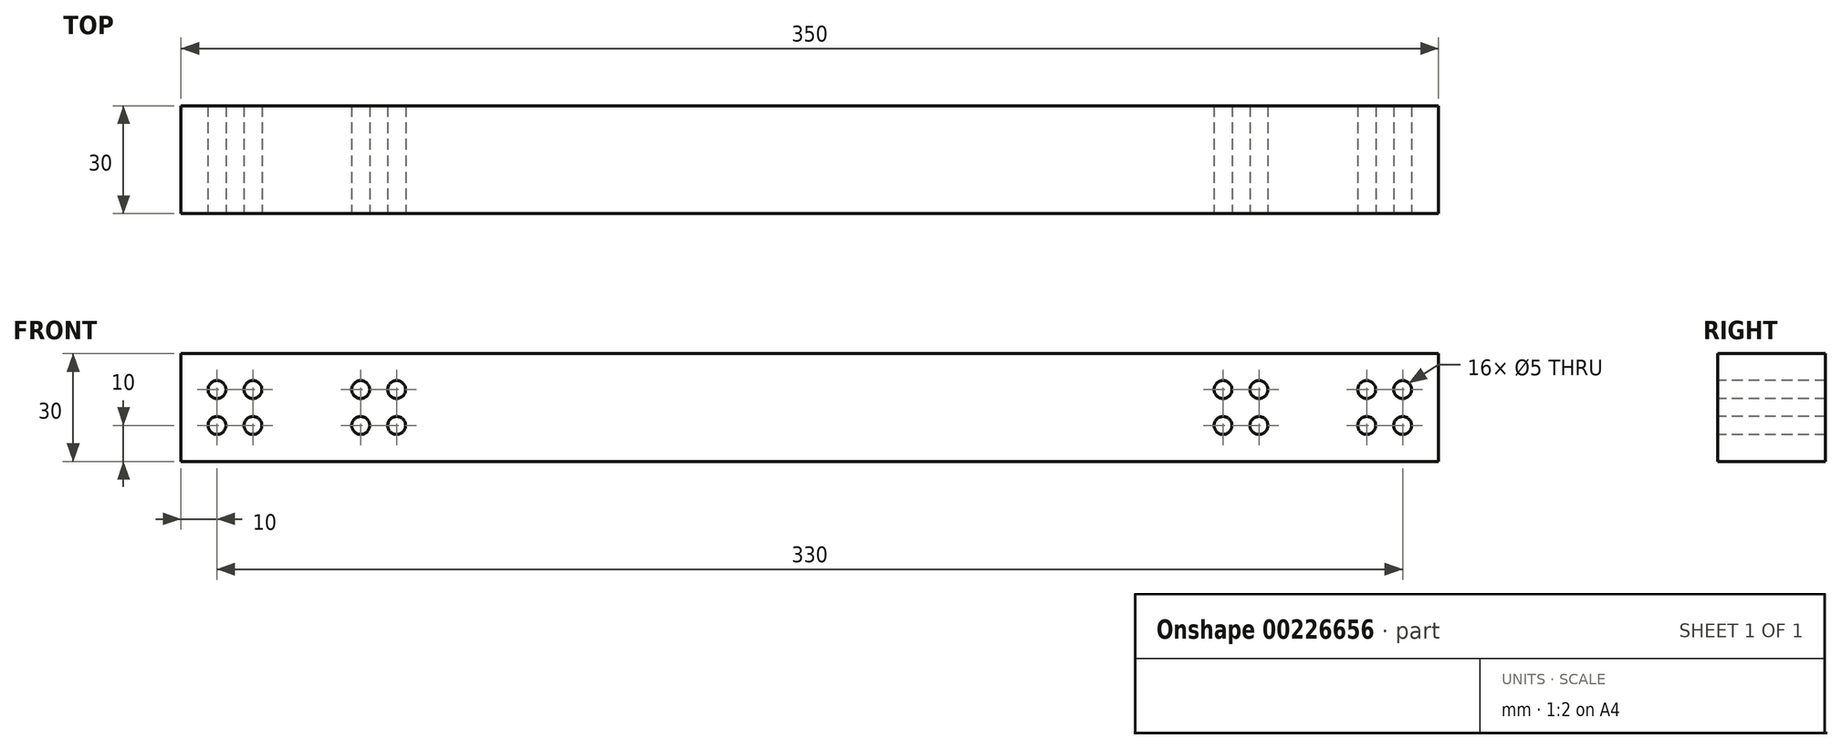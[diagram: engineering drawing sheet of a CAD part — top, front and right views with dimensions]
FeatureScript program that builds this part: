
annotation { "Feature Type Name" : "Feature", "Feature Type Description" : "" }
export const myFeature = defineFeature(function(context is Context, id is Id, definition is map)
    precondition{}
    {
        {
            var Q0;
            Q0=qCreatedBy(makeId("Front.planeOp"),FACE);
            var sketch = newSketch(context, id + "F0", { "sketchPlane" : qUnion([Q0])});
            skLineSegment(sketch, "E0.bottom", {"start": v(-175, 15) * mm, "end": v(175, 15) * mm});
            skLineSegment(sketch, "E0.top", {"start": v(-175, -15) * mm, "end": v(175, -15) * mm});
            skLineSegment(sketch, "E0.left", {"start": v(-175, 15) * mm, "end": v(-175, -15) * mm});
            skLineSegment(sketch, "E0.right", {"start": v(175, 15) * mm, "end": v(175, -15) * mm});
            skLineSegment(sketch, "E1", {"start": v(0, 15) * mm, "end": v(0, -15) * mm, "construction": true});
            skLineSegment(sketch, "E2", {"start": v(-175, 0) * mm, "end": v(175, 0) * mm, "construction": true});
            skSolve(sketch);
        }
        {
            var Q0;
            Q0=makeQuery(id+"F0.imprint","IMPRINT",FACE,{"disambiguationData":[TD([[makeQuery(id+"F0.imprint","IMPRINT",EDGE,{"derivedFrom":sQuery(id+"F0.wireOp",EDGE,"E0.bottom")}),-1.0]])]});
            extrude(context, id + "F1", {"entities" : qUnion([Q0]), "endBound" : BoundingType.SYMMETRIC, "depth" : 30 * mm});
        }
        {
            var Q0;
            Q0=makeQuery(id+"F1.opExtrude","CAP_FACE",FACE,{"disambiguationData":[OSD([sQuery(id+"F0.wireOp",EDGE,"E0.bottom"),sQuery(id+"F0.wireOp",EDGE,"E0.top"),sQuery(id+"F0.wireOp",EDGE,"E0.left"),sQuery(id+"F0.wireOp",EDGE,"E0.right")])],"isStart":false});
            var sketch = newSketch(context, id + "F2", { "sketchPlane" : qUnion([Q0])});
            skPoint(sketch, "E3", {"position": v(-165, 5) * mm});
            skPoint(sketch, "E4", {"position": v(-155, -5) * mm});
            skPoint(sketch, "E5", {"position": v(-155, 5) * mm});
            skPoint(sketch, "E6", {"position": v(-165, -5) * mm});
            skPoint(sketch, "E7", {"position": v(155, 5) * mm});
            skPoint(sketch, "E8", {"position": v(165, 5) * mm});
            skPoint(sketch, "E9", {"position": v(155, -5) * mm});
            skPoint(sketch, "E10", {"position": v(165, -5) * mm});
            skPoint(sketch, "E11", {"position": v(-125, 5) * mm});
            skPoint(sketch, "E12", {"position": v(-125, -5) * mm});
            skPoint(sketch, "E13", {"position": v(-115, -5) * mm});
            skPoint(sketch, "E14", {"position": v(-115, 5) * mm});
            skPoint(sketch, "E15", {"position": v(125, 5) * mm});
            skPoint(sketch, "E16", {"position": v(125, -5) * mm});
            skPoint(sketch, "E17", {"position": v(115, 5) * mm});
            skPoint(sketch, "E18", {"position": v(115, -5) * mm});
            skSolve(sketch);
        }
        {
            var Q0;
            Q0=sQuery(id+"F2.wireOp",VERTEX,"E3");
            var Q1;
            Q1=sQuery(id+"F2.wireOp",VERTEX,"E6");
            var Q2;
            Q2=sQuery(id+"F2.wireOp",VERTEX,"E5");
            var Q3;
            Q3=sQuery(id+"F2.wireOp",VERTEX,"E4");
            var Q4;
            Q4=sQuery(id+"F2.wireOp",VERTEX,"E7");
            var Q5;
            Q5=sQuery(id+"F2.wireOp",VERTEX,"E9");
            var Q6;
            Q6=sQuery(id+"F2.wireOp",VERTEX,"E8");
            var Q7;
            Q7=sQuery(id+"F2.wireOp",VERTEX,"E10");
            var Q8;
            Q8=sQuery(id+"F2.wireOp",VERTEX,"E11");
            var Q9;
            Q9=sQuery(id+"F2.wireOp",VERTEX,"E12");
            var Q10;
            Q10=sQuery(id+"F2.wireOp",VERTEX,"E14");
            var Q11;
            Q11=sQuery(id+"F2.wireOp",VERTEX,"E13");
            var Q12;
            Q12=sQuery(id+"F2.wireOp",VERTEX,"E17");
            var Q13;
            Q13=sQuery(id+"F2.wireOp",VERTEX,"E15");
            var Q14;
            Q14=sQuery(id+"F2.wireOp",VERTEX,"E16");
            var Q15;
            Q15=sQuery(id+"F2.wireOp",VERTEX,"E18");
            var Q16;
            Q16=makeQuery(id+"F1.opExtrude","SWEPT_BODY",BODY,{"disambiguationData":[OSD([sQuery(id+"F0.wireOp",EDGE,"E0.bottom"),sQuery(id+"F0.wireOp",EDGE,"E0.top"),sQuery(id+"F0.wireOp",EDGE,"E0.left"),sQuery(id+"F0.wireOp",EDGE,"E0.right")])]});
            hole(context, id + "F3", {"style" : HoleStyle.SIMPLE, "endStyle" : HoleEndStyle.THROUGH, "holeDiameter" : 5 * mm, "locations" : qUnion([Q0, Q1, Q2, Q3, Q4, Q5, Q6, Q7, Q8, Q9, Q10, Q11, Q12, Q13, Q14, Q15]), "scope" : qUnion([Q16]), "isTappedThrough" : true});
        }
    });
